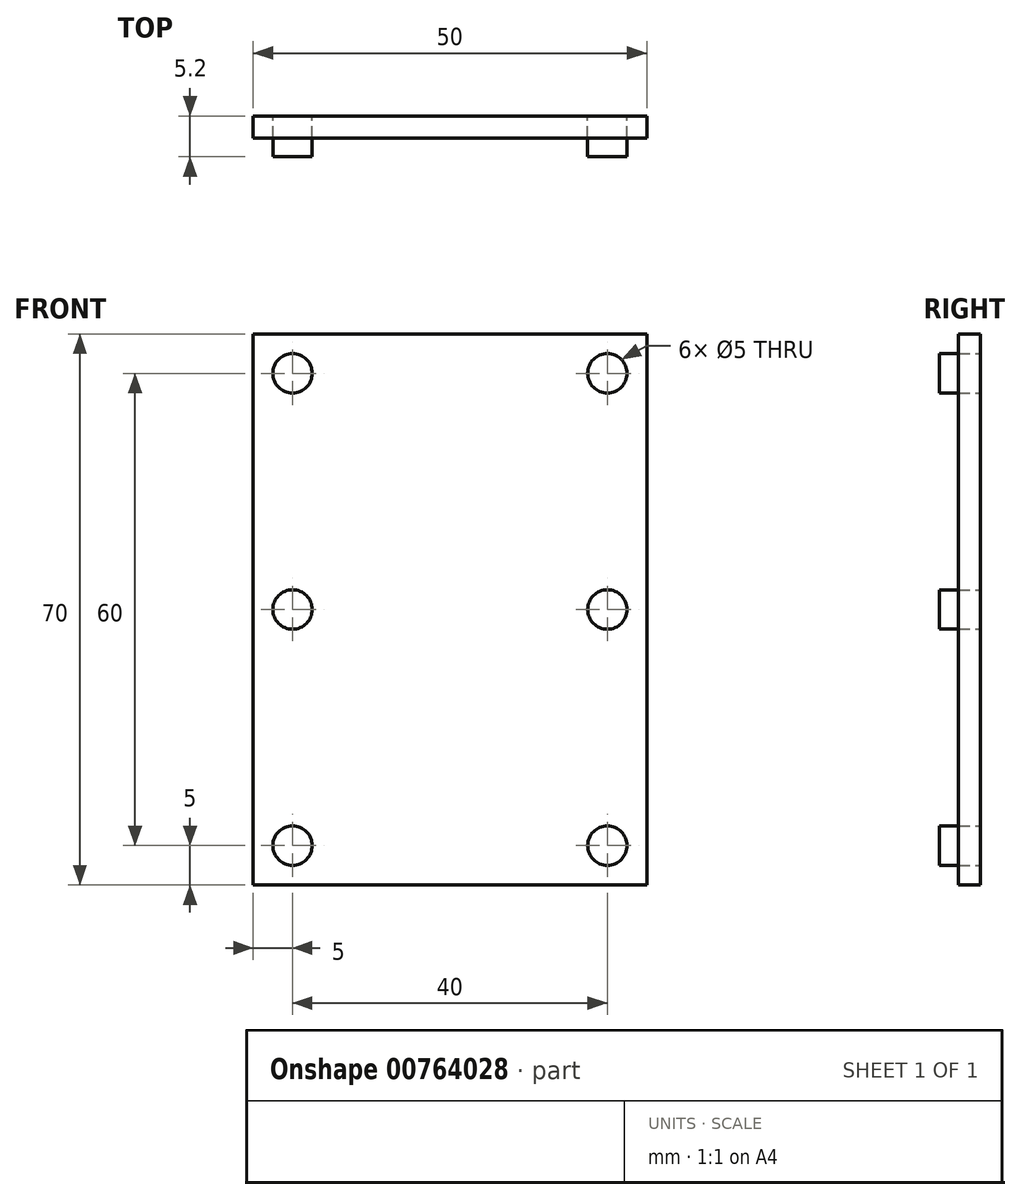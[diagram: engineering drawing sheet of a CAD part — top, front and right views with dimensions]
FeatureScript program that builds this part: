
annotation { "Feature Type Name" : "Feature", "Feature Type Description" : "" }
export const myFeature = defineFeature(function(context is Context, id is Id, definition is map)
    precondition{}
    {
        {
            var Q0;
            Q0=qCreatedBy(makeId("Front.planeOp"),FACE);
            var sketch = newSketch(context, id + "F0", { "sketchPlane" : qUnion([Q0])});
            skLineSegment(sketch, "E0.bottom", {"start": v(-25, -35) * mm, "end": v(25, -35) * mm});
            skLineSegment(sketch, "E0.top", {"start": v(-25, 35) * mm, "end": v(25, 35) * mm});
            skLineSegment(sketch, "E0.left", {"start": v(-25, -35) * mm, "end": v(-25, 35) * mm});
            skLineSegment(sketch, "E0.right", {"start": v(25, -35) * mm, "end": v(25, 35) * mm});
            skPoint(sketch, "E0.middle", {"position": v(0, 0) * mm});
            skCircle(sketch, "E1", {"center": v(20, 30) * mm, "radius": 2.5 * mm});
            skCircle(sketch, "E2", {"center": v(20, 0) * mm, "radius": 2.5 * mm});
            skCircle(sketch, "E3", {"center": v(20, -30) * mm, "radius": 2.5 * mm});
            skCircle(sketch, "E4", {"center": v(-20, 30) * mm, "radius": 2.5 * mm});
            skCircle(sketch, "E5", {"center": v(-20, 0) * mm, "radius": 2.5 * mm});
            skCircle(sketch, "E6", {"center": v(-20, -30) * mm, "radius": 2.5 * mm});
            skSolve(sketch);
        }
        {
            var Q0;
            Q0=makeQuery(id+"F0.imprint","IMPRINT",FACE,{"disambiguationData":[TD([[makeQuery(id+"F0.imprint","IMPRINT",EDGE,{"derivedFrom":sQuery(id+"F0.wireOp",EDGE,"E4")}),1.0]])]});
            var Q1;
            Q1=makeQuery(id+"F0.imprint","IMPRINT",FACE,{"disambiguationData":[TD([[makeQuery(id+"F0.imprint","IMPRINT",EDGE,{"derivedFrom":sQuery(id+"F0.wireOp",EDGE,"E1")}),1.0]])]});
            var Q2;
            Q2=makeQuery(id+"F0.imprint","IMPRINT",FACE,{"disambiguationData":[TD([[makeQuery(id+"F0.imprint","IMPRINT",EDGE,{"derivedFrom":sQuery(id+"F0.wireOp",EDGE,"E2")}),1.0]])]});
            var Q3;
            Q3=makeQuery(id+"F0.imprint","IMPRINT",FACE,{"disambiguationData":[TD([[makeQuery(id+"F0.imprint","IMPRINT",EDGE,{"derivedFrom":sQuery(id+"F0.wireOp",EDGE,"E5")}),1.0]])]});
            var Q4;
            Q4=makeQuery(id+"F0.imprint","IMPRINT",FACE,{"disambiguationData":[TD([[makeQuery(id+"F0.imprint","IMPRINT",EDGE,{"derivedFrom":sQuery(id+"F0.wireOp",EDGE,"E6")}),1.0]])]});
            var Q5;
            Q5=makeQuery(id+"F0.imprint","IMPRINT",FACE,{"disambiguationData":[TD([[makeQuery(id+"F0.imprint","IMPRINT",EDGE,{"derivedFrom":sQuery(id+"F0.wireOp",EDGE,"E3")}),1.0]])]});
            extrude(context, id + "F1", {"entities" : qUnion([Q0, Q1, Q2, Q3, Q4, Q5]), "depth" : 5.2 * mm, "offsetDistance" : 25 * mm});
        }
        {
            var Q0;
            Q0=makeQuery(id+"F0.imprint","IMPRINT",FACE,{"disambiguationData":[TD([[makeQuery(id+"F0.imprint","IMPRINT",EDGE,{"derivedFrom":sQuery(id+"F0.wireOp",EDGE,"E0.bottom")}),1.0]])]});
            extrude(context, id + "F2", {"entities" : qUnion([Q0]), "depth" : 2.8 * mm, "offsetDistance" : 25 * mm});
        }
    });
